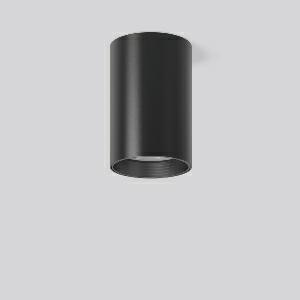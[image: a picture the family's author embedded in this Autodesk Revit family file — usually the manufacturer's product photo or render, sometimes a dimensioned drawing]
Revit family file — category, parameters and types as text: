
# Revit family: heledon_maxi_a_931220_003_3_1304
name_source: partatom
category: Lighting Fixtures
units: mm (PartAtom-declared; Revit-internal decimal feet)

## family parameters
Cut with Voids When Loaded = No
Host = Face
Light Source = No
Part Type = Normal
Room Calculation Point = No
Round Connector Dimension = Use Diameter
Shared = No

## types (1)
- HELEDON maxi A (1 x LED Modul 935, 2900 lm, 3500)
    Apparent Load = 25 VA
    Approval mark = CE
    CIE Flux Codes = 97 100 100 100 100
    Color Rendering = 92
    Color Temperature = 3500
    Default Elevation = 1800 mm
    Description = Series: HELEDON maxi
Cylindrical surface-mounted downlight. Housing: die-cast aluminium, powder-coated. Internal ceiling frame polycarbonate with bayonet mounting. Black plastic ring and recessed LED to prevent glare from the side. Optical assembly with lens made of plastic (polycarbonate) for the best homogeneous light distribution - can be changed without tools. Best colour rendering index Ra>90. Suitable for Ceiling mounting. Easy installation with a separate ceiling frame with bayonet mounting and plug connection. Driver integrated. Connected via plug-in connector. High quality converter without flickering and stroboscopic effect. The following accessories can be mounted without use of tools: interchangeable lenses, decorative glasses, honeycomb louvre, clear and frosted diffusers, white interchangeable plastic ring. 
Colour: deep black, matt (RAL 9005)
Diameter: 123 mm
Height: 183 mm
Lamp: LED
Socket: without socket
Colour temperature: 3500K
Colour rendering index (CRI): 92
System power: 25 W
Rated luminous flux: 2900 lm
Luminous efficiency: 116 lm/W
Control gear: Regulated power supply
Protection class: I
Type of protection: IP 20
    Height = 183 mm
    Lamp = 1 x LED Modul 935
    Lamp Light Flux = 2900 lm
    Lamp count = 1
    Length = 123 mm
    Lifetime = 50000 h
    Luminous efficacy = 116 lm/W
    Manufacturer = RZB
    ModVariant = No
    Model = 931220.003.3
    Mounting Place = Ceiling
    Mounting Type = Surface mounted
    Number of Poles = 1
    OnlyDefault = Yes
    Power Factor = 1
    Product Name = HELEDON maxi A
    Product group = Surface mounted downlights
    ProductGroupID = 302
    Protection Class = Protection class I
    Protection Degree = IP 20
    RLX_Detail_Level = 1
    RLX_Emergency_Light_Flux = 0 lm
    RLX_Emergency_Type = 0
    RLX_Emergency_Type_DB = No
    RlxData = <blob elided: 97797 chars, md5=1dfa6925>
    Socket = socket
    Standby Power = 0 W
    System Light Flux = 2900 lm
    System Power = 25 W
    Type Comments = Product without accessories
    Type Image = 931193.003.jpg
    URL = http://relux.com
    VarID = ---
    Voltage = 230 V
    Voltage Range = 220-240 V
    Weight = 0.00 kg
    Width = 0 mm  [stored 0 ft]

note: [stored X ft] marks values corroborated as IEEE doubles in the binary element streams (Revit-internal decimal feet)

## geometry (parser evidence)
native form markers: Blend x4, Sweep x10
no freeform markers — native parametric forms only
